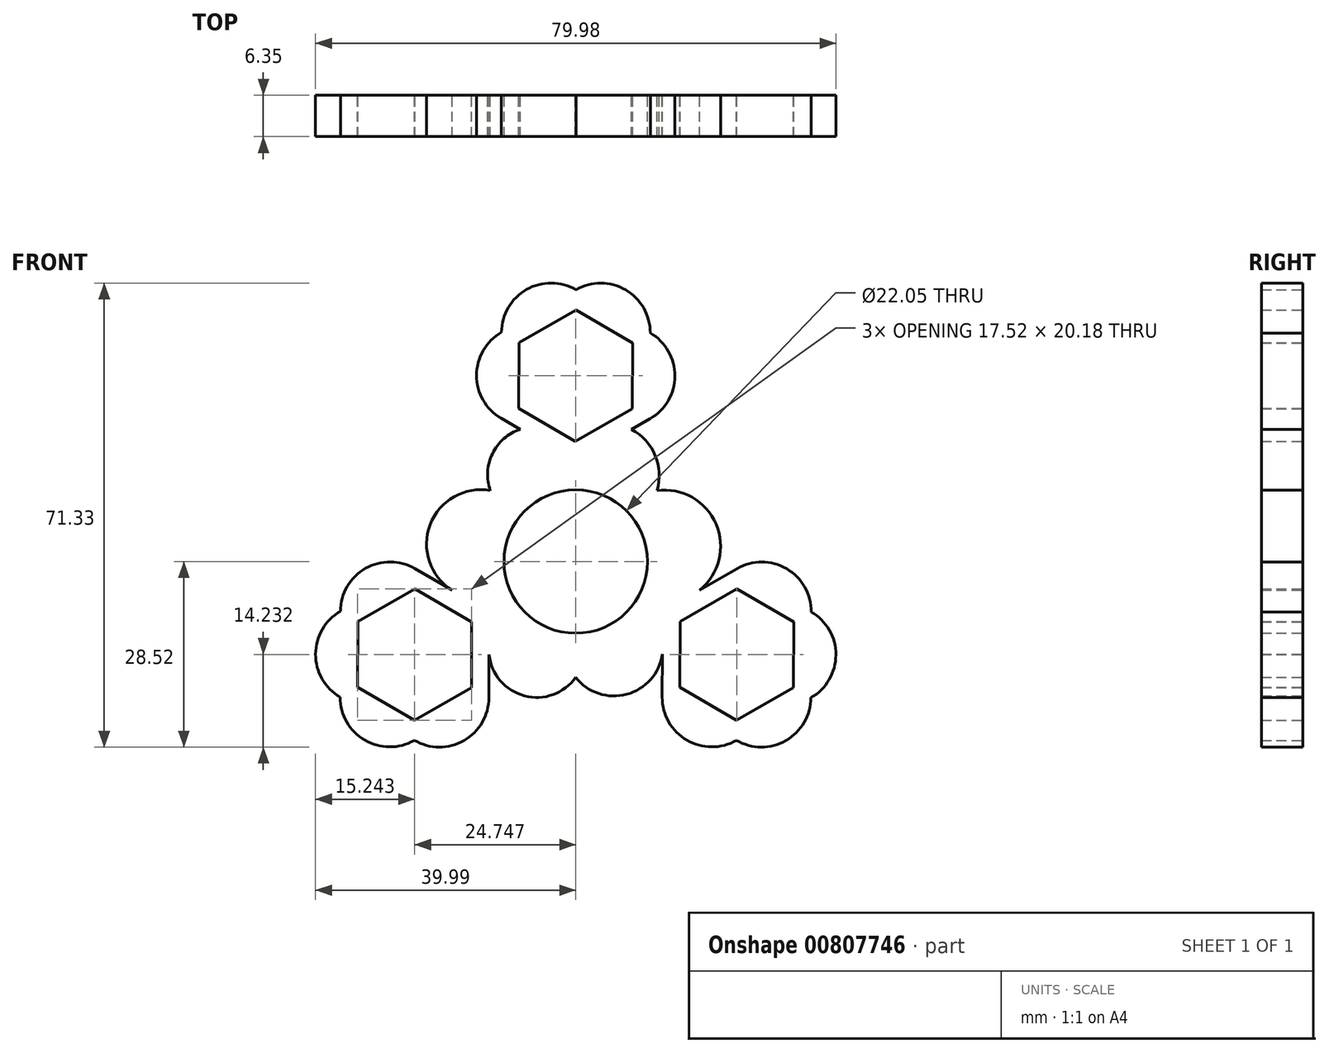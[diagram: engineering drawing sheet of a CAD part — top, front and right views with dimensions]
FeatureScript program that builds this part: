
annotation { "Feature Type Name" : "Feature", "Feature Type Description" : "" }
export const myFeature = defineFeature(function(context is Context, id is Id, definition is map)
    precondition{}
    {
        {
            var Q0;
            Q0=qCreatedBy(makeId("Front.planeOp"),FACE);
            var sketch = newSketch(context, id + "F0", { "sketchPlane" : qUnion([Q0])});
            skCircle(sketch, "E0", {"center": v(0, 0) * mm, "radius": 11.02 * mm});
            skCircle(sketch, "E1", {"center": v(0, 0) * mm, "radius": 14.29 * mm});
            skCircle(sketch, "E2.cCircle", {"center": v(0, 28.58) * mm, "radius": 8.74 * mm, "construction": true});
            skLineSegment(sketch, "E2.0", {"start": v(-8.72, 33.65) * mm, "end": v(0.04, 38.66) * mm});
            skLineSegment(sketch, "E2.1", {"start": v(0.04, 38.66) * mm, "end": v(8.76, 33.58) * mm});
            skLineSegment(sketch, "E2.2", {"start": v(8.76, 33.58) * mm, "end": v(8.72, 23.5) * mm});
            skLineSegment(sketch, "E2.3", {"start": v(8.72, 23.5) * mm, "end": v(-0.04, 18.49) * mm});
            skLineSegment(sketch, "E2.4", {"start": v(-0.04, 18.49) * mm, "end": v(-8.76, 23.57) * mm});
            skLineSegment(sketch, "E2.5", {"start": v(-8.76, 23.57) * mm, "end": v(-8.72, 33.65) * mm});
            skPoint(sketch, "E2.0.midPoint", {"position": v(-4.34, 36.16) * mm});
            skCircle(sketch, "E3.cCircle", {"center": v(0, 28.58) * mm, "radius": 11.43 * mm, "construction": true});
            skLineSegment(sketch, "E3.0", {"start": v(-11.4, 35.22) * mm, "end": v(0.05, 41.77) * mm});
            skLineSegment(sketch, "E3.1", {"start": v(0.05, 41.77) * mm, "end": v(11.46, 35.13) * mm});
            skLineSegment(sketch, "E3.2", {"start": v(11.46, 35.13) * mm, "end": v(11.4, 21.93) * mm});
            skLineSegment(sketch, "E3.3", {"start": v(11.4, 21.93) * mm, "end": v(-0.05, 15.38) * mm});
            skLineSegment(sketch, "E3.4", {"start": v(-0.05, 15.38) * mm, "end": v(-11.46, 22.02) * mm});
            skLineSegment(sketch, "E3.5", {"start": v(-11.46, 22.02) * mm, "end": v(-11.4, 35.22) * mm});
            skPoint(sketch, "E3.0.midPoint", {"position": v(-5.68, 38.5) * mm});
            skLineSegment(sketch, "E4.1.0", {"start": v(-24.7, -4.2) * mm, "end": v(-15.99, -9.28) * mm});
            skLineSegment(sketch, "E4.1.1", {"start": v(-15.99, -9.28) * mm, "end": v(-16.03, -19.37) * mm});
            skLineSegment(sketch, "E4.1.2", {"start": v(-16.03, -19.37) * mm, "end": v(-24.79, -24.38) * mm});
            skCircle(sketch, "E4.1.3", {"center": v(-24.75, -14.29) * mm, "radius": 11.43 * mm, "construction": true});
            skLineSegment(sketch, "E4.1.4", {"start": v(-33.5, -19.3) * mm, "end": v(-33.46, -9.2) * mm});
            skLineSegment(sketch, "E4.1.5", {"start": v(-24.8, -27.49) * mm, "end": v(-36.2, -20.84) * mm});
            skLineSegment(sketch, "E4.1.6", {"start": v(-36.2, -20.84) * mm, "end": v(-36.15, -7.64) * mm});
            skLineSegment(sketch, "E4.1.7", {"start": v(-36.15, -7.64) * mm, "end": v(-24.7, -1.09) * mm});
            skPoint(sketch, "E4.1.8", {"position": v(-29.15, -21.84) * mm});
            skLineSegment(sketch, "E4.1.9", {"start": v(-33.46, -9.2) * mm, "end": v(-24.7, -4.2) * mm});
            skLineSegment(sketch, "E4.1.10", {"start": v(-24.79, -24.38) * mm, "end": v(-33.5, -19.3) * mm});
            skCircle(sketch, "E4.1.11", {"center": v(-24.75, -14.29) * mm, "radius": 8.74 * mm, "construction": true});
            skPoint(sketch, "E4.1.12", {"position": v(-30.5, -24.16) * mm});
            skLineSegment(sketch, "E4.1.13", {"start": v(-13.34, -20.93) * mm, "end": v(-24.8, -27.49) * mm});
            skLineSegment(sketch, "E4.1.14", {"start": v(-13.3, -7.73) * mm, "end": v(-13.34, -20.93) * mm});
            skLineSegment(sketch, "E4.1.15", {"start": v(-24.7, -1.09) * mm, "end": v(-13.3, -7.73) * mm});
            skLineSegment(sketch, "E4.2.0", {"start": v(15.99, -19.3) * mm, "end": v(16.03, -9.2) * mm});
            skLineSegment(sketch, "E4.2.1", {"start": v(16.03, -9.2) * mm, "end": v(24.79, -4.2) * mm});
            skLineSegment(sketch, "E4.2.2", {"start": v(24.79, -4.2) * mm, "end": v(33.5, -9.28) * mm});
            skCircle(sketch, "E4.2.3", {"center": v(24.75, -14.29) * mm, "radius": 11.43 * mm, "construction": true});
            skLineSegment(sketch, "E4.2.4", {"start": v(33.46, -19.37) * mm, "end": v(24.7, -24.38) * mm});
            skLineSegment(sketch, "E4.2.5", {"start": v(36.2, -7.73) * mm, "end": v(36.15, -20.93) * mm});
            skLineSegment(sketch, "E4.2.6", {"start": v(36.15, -20.93) * mm, "end": v(24.7, -27.49) * mm});
            skLineSegment(sketch, "E4.2.7", {"start": v(24.7, -27.49) * mm, "end": v(13.3, -20.84) * mm});
            skPoint(sketch, "E4.2.8", {"position": v(33.48, -14.32) * mm});
            skLineSegment(sketch, "E4.2.9", {"start": v(24.7, -24.38) * mm, "end": v(15.99, -19.3) * mm});
            skLineSegment(sketch, "E4.2.10", {"start": v(33.5, -9.28) * mm, "end": v(33.46, -19.37) * mm});
            skCircle(sketch, "E4.2.11", {"center": v(24.75, -14.29) * mm, "radius": 8.74 * mm, "construction": true});
            skPoint(sketch, "E4.2.12", {"position": v(36.18, -14.33) * mm});
            skLineSegment(sketch, "E4.2.13", {"start": v(24.8, -1.09) * mm, "end": v(36.2, -7.73) * mm});
            skLineSegment(sketch, "E4.2.14", {"start": v(13.34, -7.64) * mm, "end": v(24.8, -1.09) * mm});
            skLineSegment(sketch, "E4.2.15", {"start": v(13.3, -20.84) * mm, "end": v(13.34, -7.64) * mm});
            skArc(sketch, "E5", {"start": v(-13.13, 10.91) * mm, "mid": v(-22.38, 5.67) * mm, "end": v(-19, -4.41) * mm});
            skArc(sketch, "E6", {"start": v(19.07, -4.37) * mm, "mid": v(21.57, 5.77) * mm, "end": v(12.5, 10.91) * mm});
            skArc(sketch, "E7", {"start": v(-8.53, 20.32) * mm, "mid": v(-12.8, 16.58) * mm, "end": v(-13.13, 10.91) * mm});
            skArc(sketch, "E8", {"start": v(12.5, 10.91) * mm, "mid": v(12.2, 16.3) * mm, "end": v(8.59, 20.32) * mm});
            skArc(sketch, "E9", {"start": v(-13.32, -14.33) * mm, "mid": v(-7.85, -20.66) * mm, "end": v(0, -17.8) * mm});
            skArc(sketch, "E10", {"start": v(0, -17.8) * mm, "mid": v(7.83, -20.4) * mm, "end": v(13.32, -14.24) * mm});
            skArc(sketch, "E11", {"start": v(-36.2, -20.84) * mm, "mid": v(-32.42, -27.46) * mm, "end": v(-24.8, -27.49) * mm});
            skArc(sketch, "E12", {"start": v(-24.8, -27.49) * mm, "mid": v(-17.18, -27.52) * mm, "end": v(-13.34, -20.93) * mm});
            skArc(sketch, "E13", {"start": v(-36.15, -7.64) * mm, "mid": v(-39.99, -14.23) * mm, "end": v(-36.2, -20.84) * mm});
            skArc(sketch, "E14", {"start": v(-24.7, -1.09) * mm, "mid": v(-32.31, -1.06) * mm, "end": v(-36.15, -7.64) * mm});
            skArc(sketch, "E15", {"start": v(13.3, -20.84) * mm, "mid": v(17.07, -27.46) * mm, "end": v(24.7, -27.49) * mm});
            skArc(sketch, "E16", {"start": v(24.7, -27.49) * mm, "mid": v(32.31, -27.52) * mm, "end": v(36.15, -20.93) * mm});
            skArc(sketch, "E17", {"start": v(36.15, -20.93) * mm, "mid": v(39.99, -14.35) * mm, "end": v(36.2, -7.73) * mm});
            skArc(sketch, "E18", {"start": v(36.2, -7.73) * mm, "mid": v(32.42, -1.12) * mm, "end": v(24.8, -1.09) * mm});
            skArc(sketch, "E19", {"start": v(11.46, 35.13) * mm, "mid": v(7.67, 41.74) * mm, "end": v(0.05, 41.77) * mm});
            skArc(sketch, "E20", {"start": v(11.4, 21.93) * mm, "mid": v(15.24, 28.51) * mm, "end": v(11.46, 35.13) * mm});
            skArc(sketch, "E21", {"start": v(0.05, 41.77) * mm, "mid": v(-7.57, 41.8) * mm, "end": v(-11.4, 35.22) * mm});
            skArc(sketch, "E22", {"start": v(-11.4, 35.22) * mm, "mid": v(-15.24, 28.64) * mm, "end": v(-11.46, 22.02) * mm});
            skSolve(sketch);
        }
        {
            var Q0;
            Q0 = qSketchRegion(id + "F0", true);
            var Q1;
            Q1=makeQuery(id+"F0.imprint","IMPRINT",FACE,{"disambiguationData":[TD([[makeQuery(id+"F0.imprint","IMPRINT",EDGE,{"derivedFrom":sQuery(id+"F0.wireOp",EDGE,"E0")}),-1.0]])]});
            extrude(context, id + "F1", {"entities" : qUnion([Q0, Q1]), "depth" : 6.35 * mm, "offsetDistance" : 25.4 * mm});
        }
    });
